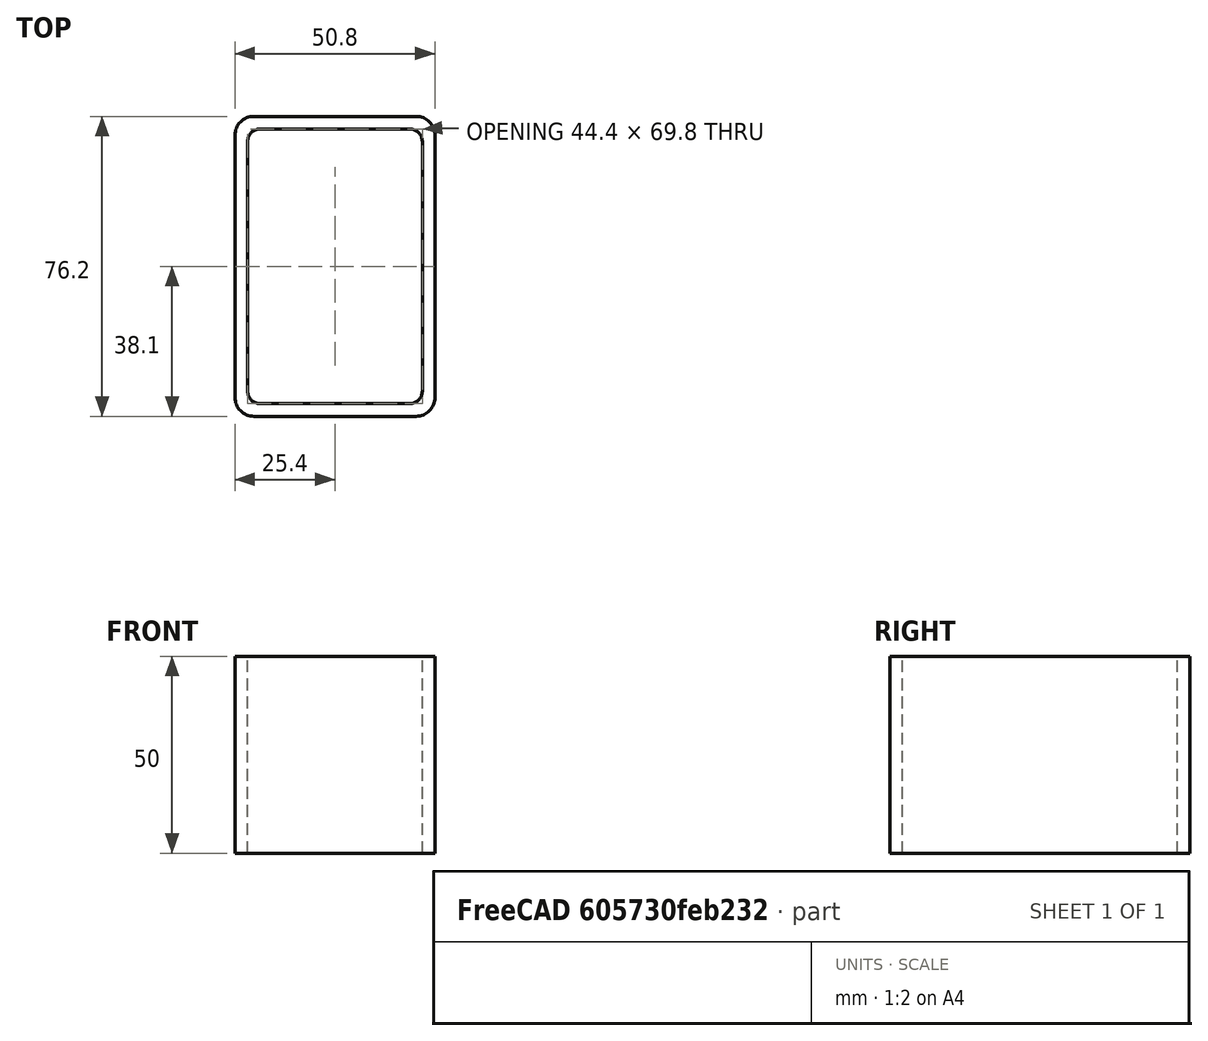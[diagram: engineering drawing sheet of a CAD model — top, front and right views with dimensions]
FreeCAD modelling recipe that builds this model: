
FCSTD DOCUMENT  (FreeCAD 0.15R4671 (Git))
Label: Rectangular hollow section 76.2 x50.8 x3.2 EN10219 S235JRH
License: All rights reserved
LicenseURL: http://en.wikipedia.org/wiki/All_rights_reserved
objects: Sketcher::SketchObject×1, Part::Extrusion×1
note: 2 computed .brp shape members not serialized (recipe doc carries the construction recipe); baked Part::Feature solids carry a one-line shape summary decoded from their .brp

FEATURE [Sketcher::SketchObject] Sketch
  sketch-geometry (16):
    g0: LineSegment StartX=-19 StartY=34.9 StartZ=0 EndX=19 EndY=34.9 EndZ=0
    g1: LineSegment StartX=22.2 StartY=31.7 StartZ=0 EndX=22.2 EndY=-31.7 EndZ=0
    g2: LineSegment StartX=19 StartY=-34.9 StartZ=0 EndX=-19 EndY=-34.9 EndZ=0
    g3: LineSegment StartX=-22.2 StartY=-31.7 StartZ=0 EndX=-22.2 EndY=31.7 EndZ=0
    g4: LineSegment StartX=-20.6 StartY=38.1 StartZ=0 EndX=20.6 EndY=38.1 EndZ=0
    g5: LineSegment StartX=25.4 StartY=33.3 StartZ=0 EndX=25.4 EndY=-33.3 EndZ=0
    g6: LineSegment StartX=20.6 StartY=-38.1 StartZ=0 EndX=-20.6 EndY=-38.1 EndZ=0
    g7: LineSegment StartX=-25.4 StartY=-33.3 StartZ=0 EndX=-25.4 EndY=33.3 EndZ=0
    g8: ArcOfCircle CenterX=-19 CenterY=31.7 CenterZ=0 NormalX=0 NormalY=0 NormalZ=1 Radius=3.2 StartAngle=1.5708 EndAngle=3.14159
    g9: ArcOfCircle CenterX=19 CenterY=31.7 CenterZ=0 NormalX=0 NormalY=0 NormalZ=1 Radius=3.2 StartAngle=0 EndAngle=1.5708
    g10: ArcOfCircle CenterX=19 CenterY=-31.7 CenterZ=0 NormalX=0 NormalY=0 NormalZ=1 Radius=3.2 StartAngle=4.71239 EndAngle=6.28319
    g11: ArcOfCircle CenterX=-19 CenterY=-31.7 CenterZ=0 NormalX=0 NormalY=0 NormalZ=1 Radius=3.2 StartAngle=3.14159 EndAngle=4.71239
    g12: ArcOfCircle CenterX=20.6 CenterY=33.3 CenterZ=0 NormalX=0 NormalY=0 NormalZ=1 Radius=4.8 StartAngle=0 EndAngle=1.5708
    g13: ArcOfCircle CenterX=20.6 CenterY=-33.3 CenterZ=0 NormalX=0 NormalY=0 NormalZ=1 Radius=4.8 StartAngle=4.71239 EndAngle=6.28319
    g14: ArcOfCircle CenterX=-20.6 CenterY=-33.3 CenterZ=0 NormalX=0 NormalY=0 NormalZ=1 Radius=4.8 StartAngle=3.14159 EndAngle=4.71239
    g15: ArcOfCircle CenterX=-20.6 CenterY=33.3 CenterZ=0 NormalX=0 NormalY=0 NormalZ=1 Radius=4.8 StartAngle=1.5708 EndAngle=3.14159
  constraints (36):
    c: Horizontal(g2)
    c: Vertical(g3)
    c: Horizontal(g6)
    c: Vertical(g7)
    c: Tangent(g3,g8) = 1.5708
    c: Tangent(g0,g8) = 1.5708
    c: Tangent(g0,g9) = 1.5708
    c: Tangent(g1,g9) = 1.5708
    c: Tangent(g1,g10) = 1.5708
    c: Tangent(g2,g10) = 1.5708
    c: Tangent(g2,g11) = 1.5708
    c: Tangent(g3,g11) = 1.5708
    c: Tangent(g4,g12) = 1.5708
    c: Tangent(g5,g12) = 1.5708
    c: Tangent(g5,g13) = 1.5708
    c: Tangent(g6,g13) = 1.5708
    c: Tangent(g6,g14) = 1.5708
    c: Tangent(g7,g14) = 1.5708
    c: Tangent(g7,g15) = 1.5708
    c: Tangent(g4,g15) = 1.5708
    c: Equal(g9,g8)
    c: Equal(g9,g11)
    c: Equal(g9,g10)
    c: Equal(g12,g15)
    c: Equal(g12,g14)
    c: Equal(g12,g13)
    c: Symmetric(g4,g6,g-1)
    c: Symmetric(g7,g5,g-2)
    c: DistanceY(g4,g6) = -76.2
    c: DistanceX(g7,g5) = 50.8
    c: Symmetric(g3,g1,g-2)
    c: Symmetric(g0,g2,g-1)
    c: DistanceY(g0,g4) = 3.2
    c: DistanceX(g5,g1) = -3.2
    c: Radius(g9) = 3.2
    c: Radius(g12) = 4.8
FEATURE [Part::Extrusion] Extrude  label="Rectangular hollow section 76.2 x50.8 x3.2 EN10219 S235JRH"
  Base = -> Sketch
  Dir = (0,0,50)
  Solid = true
